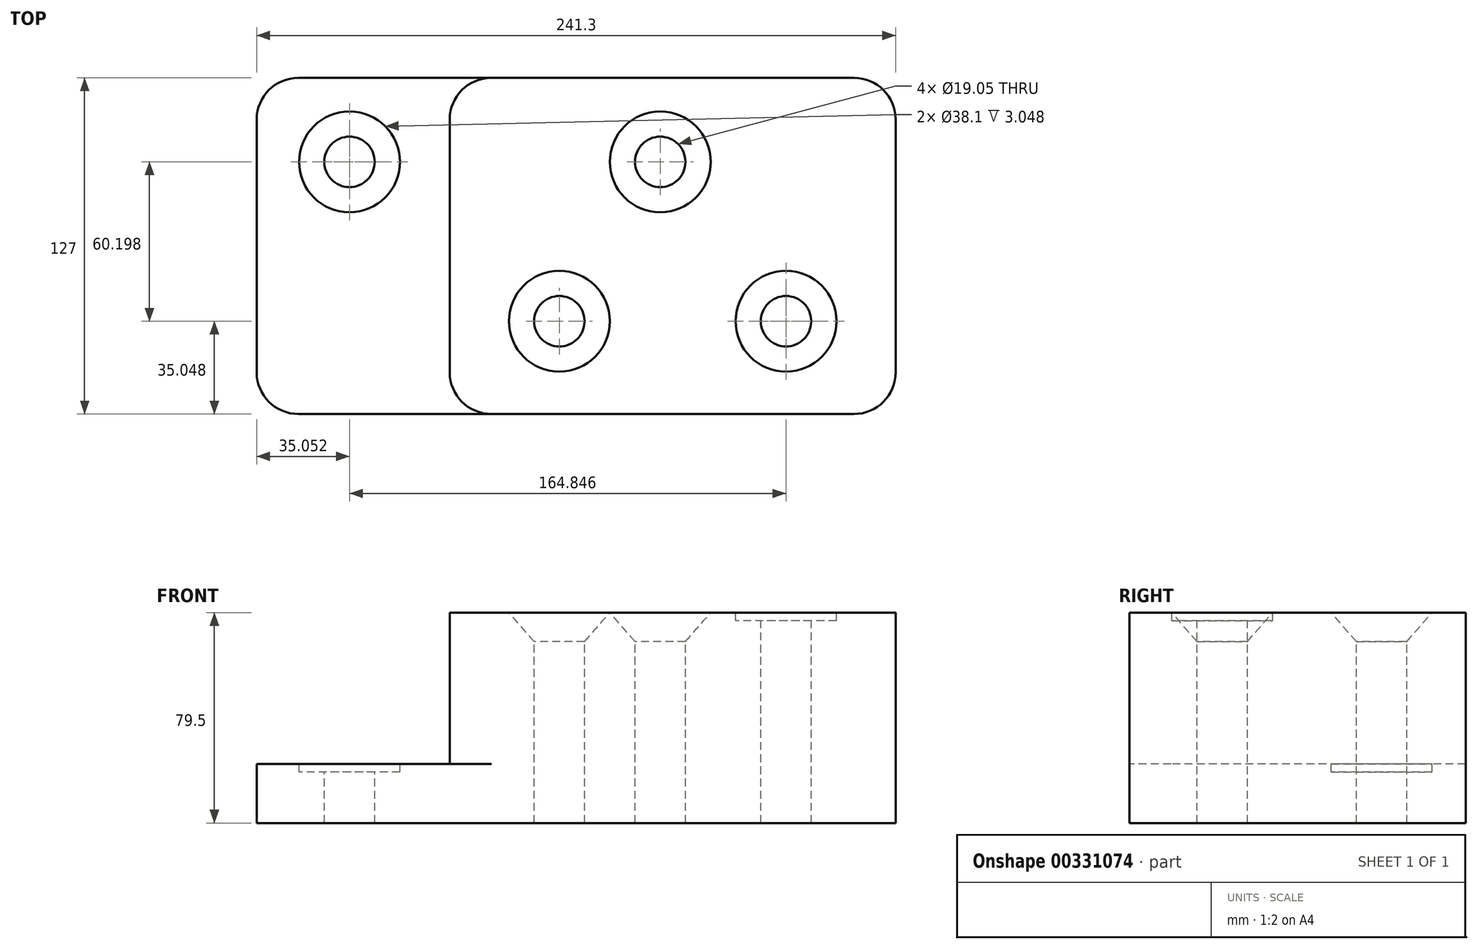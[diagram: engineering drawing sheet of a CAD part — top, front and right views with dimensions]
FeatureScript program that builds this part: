
annotation { "Feature Type Name" : "Feature", "Feature Type Description" : "" }
export const myFeature = defineFeature(function(context is Context, id is Id, definition is map)
    precondition{}
    {
        {
            var Q0;
            Q0=qCreatedBy(makeId("Top.planeOp"),FACE);
            var sketch = newSketch(context, id + "F0", { "sketchPlane" : qUnion([Q0])});
            skLineSegment(sketch, "E0.bottom", {"start": v(-178.85, 101.87) * mm, "end": v(62.45, 101.87) * mm});
            skLineSegment(sketch, "E0.top", {"start": v(-178.85, -25.13) * mm, "end": v(62.45, -25.13) * mm});
            skLineSegment(sketch, "E0.left", {"start": v(-178.85, 101.87) * mm, "end": v(-178.85, -25.13) * mm});
            skLineSegment(sketch, "E0.right", {"start": v(62.45, 101.87) * mm, "end": v(62.45, -25.13) * mm});
            skSolve(sketch);
        }
        {
            var Q0;
            Q0 = qSketchRegion(id + "F0", true);
            extrude(context, id + "F1", {"entities" : qUnion([Q0]), "depth" : 22.35 * mm});
        }
        {
            var Q0;
            Q0=makeQuery(id+"F1.opExtrude","CAP_FACE",FACE,{"disambiguationData":[OSD([sQuery(id+"F0.wireOp",EDGE,"E0.bottom"),sQuery(id+"F0.wireOp",EDGE,"E0.top"),sQuery(id+"F0.wireOp",EDGE,"E0.left"),sQuery(id+"F0.wireOp",EDGE,"E0.right")])],"isStart":false});
            var sketch = newSketch(context, id + "F2", { "sketchPlane" : qUnion([Q0])});
            skLineSegment(sketch, "E1", {"start": v(62.45, 101.87) * mm, "end": v(-105.95, 101.87) * mm});
            skLineSegment(sketch, "E2", {"start": v(-105.95, 101.87) * mm, "end": v(-105.95, -25.13) * mm});
            skLineSegment(sketch, "E3", {"start": v(-105.95, -25.13) * mm, "end": v(62.45, -25.13) * mm});
            skLineSegment(sketch, "E4", {"start": v(62.45, -25.13) * mm, "end": v(62.45, 101.87) * mm});
            skSolve(sketch);
        }
        {
            var Q0;
            Q0 = qSketchRegion(id + "F2", true);
            extrude(context, id + "F3", {"entities" : qUnion([Q0]), "operationType" : NewBodyOperationType.ADD, "depth" : 57.15 * mm});
        }
        {
            var Q0;
            Q0=makeQuery(id+"F1.opExtrude","CAP_FACE",FACE,{"disambiguationData":[OSD([sQuery(id+"F0.wireOp",EDGE,"E0.bottom"),sQuery(id+"F0.wireOp",EDGE,"E0.top"),sQuery(id+"F0.wireOp",EDGE,"E0.left"),sQuery(id+"F0.wireOp",EDGE,"E0.right")])],"isStart":false});
            var sketch = newSketch(context, id + "F4", { "sketchPlane" : qUnion([Q0])});
            skPoint(sketch, "E5", {"position": v(-143.8, 70.12) * mm});
            skSolve(sketch);
        }
        {
            var Q0;
            Q0=makeQuery(id+"F3.opExtrude","CAP_FACE",FACE,{"disambiguationData":[OSD([sQuery(id+"F2.wireOp",EDGE,"E1"),sQuery(id+"F2.wireOp",EDGE,"E2"),sQuery(id+"F2.wireOp",EDGE,"E3"),sQuery(id+"F2.wireOp",EDGE,"E4")])],"isStart":false});
            var sketch = newSketch(context, id + "F5", { "sketchPlane" : qUnion([Q0])});
            skPoint(sketch, "E6", {"position": v(-26.45, 70.12) * mm});
            skPoint(sketch, "E7", {"position": v(-64.55, 9.92) * mm});
            skPoint(sketch, "E8", {"position": v(21.05, 9.92) * mm});
            skSolve(sketch);
        }
        {
            var Q0;
            Q0=sQuery(id+"F4.wireOp",VERTEX,"E5");
            var Q1;
            Q1=sQuery(id+"F5.wireOp",VERTEX,"E8");
            var Q2;
            Q2=makeQuery(id+"F1.opExtrude","SWEPT_BODY",BODY,{"disambiguationData":[OSD([sQuery(id+"F0.wireOp",EDGE,"E0.bottom"),sQuery(id+"F0.wireOp",EDGE,"E0.top"),sQuery(id+"F0.wireOp",EDGE,"E0.left"),sQuery(id+"F0.wireOp",EDGE,"E0.right")])]});
            hole(context, id + "F6", {"style" : HoleStyle.C_BORE, "endStyle" : HoleEndStyle.THROUGH, "holeDiameter" : 19.05 * mm, "cBoreDiameter" : 38.1 * mm, "cBoreDepth" : 3.05 * mm, "tappedDepth" : 12.7 * mm, "tapClearance" : 3, "locations" : qUnion([Q0, Q1]), "scope" : qUnion([Q2])});
        }
        {
            var Q0;
            Q0=sQuery(id+"F5.wireOp",VERTEX,"E6");
            var Q1;
            Q1=sQuery(id+"F5.wireOp",VERTEX,"E7");
            var Q2;
            Q2=makeQuery(id+"F1.opExtrude","SWEPT_BODY",BODY,{"disambiguationData":[OSD([sQuery(id+"F0.wireOp",EDGE,"E0.bottom"),sQuery(id+"F0.wireOp",EDGE,"E0.top"),sQuery(id+"F0.wireOp",EDGE,"E0.left"),sQuery(id+"F0.wireOp",EDGE,"E0.right")])]});
            hole(context, id + "F7", {"style" : HoleStyle.C_SINK, "endStyle" : HoleEndStyle.THROUGH, "holeDiameter" : 19.05 * mm, "cSinkDiameter" : 38.1 * mm, "cSinkAngle" : 82 * degree, "tappedDepth" : 12.7 * mm, "tapClearance" : 3, "locations" : qUnion([Q0, Q1]), "scope" : qUnion([Q2])});
        }
        {
            var Q0;
            Q0=makeQuery(id+"F3.opExtrude","SWEPT_EDGE",EDGE,{"disambiguationData":[OSD([sQuery(id+"F0.wireOp",EDGE,"E0.top"),sQuery(id+"F2.wireOp",EDGE,"E2"),sQuery(id+"F2.wireOp",EDGE,"E3")])]});
            var Q1;
            Q1=makeQuery(id+"F3.opExtrude","SWEPT_EDGE",EDGE,{"disambiguationData":[OSD([sQuery(id+"F0.wireOp",EDGE,"E0.bottom"),sQuery(id+"F2.wireOp",EDGE,"E1"),sQuery(id+"F2.wireOp",EDGE,"E2")])]});
            var Q2;
            Q2=makeQuery(id+"F1.opExtrude","SWEPT_EDGE",EDGE,{"disambiguationData":[OSD([sQuery(id+"F0.wireOp",EDGE,"E0.bottom"),sQuery(id+"F0.wireOp",EDGE,"E0.left")])]});
            var Q3;
            Q3=makeQuery(id+"F1.opExtrude","SWEPT_EDGE",EDGE,{"disambiguationData":[OSD([sQuery(id+"F0.wireOp",EDGE,"E0.top"),sQuery(id+"F0.wireOp",EDGE,"E0.left")])]});
            fillet(context, id + "F8", {"entities" : qUnion([Q0, Q1, Q2, Q3]), "radius" : 15.75 * mm, "tangentPropagation" : true, "allowEdgeOverflow" : false});
        }
        {
            var Q0;
            Q0=makeQuery(id+"F3.boolean.opBoolean","MERGE",EDGE,{"derivedFrom":[makeQuery(id+"F1.opExtrude","SWEPT_EDGE",EDGE,{"disambiguationData":[OSD([sQuery(id+"F0.wireOp",EDGE,"E0.top"),sQuery(id+"F0.wireOp",EDGE,"E0.right")])]}),makeQuery(id+"F3.opExtrude","SWEPT_EDGE",EDGE,{"disambiguationData":[OSD([sQuery(id+"F2.wireOp",EDGE,"E3"),sQuery(id+"F2.wireOp",EDGE,"E4")])]})]});
            var Q1;
            Q1=makeQuery(id+"F3.boolean.opBoolean","MERGE",EDGE,{"derivedFrom":[makeQuery(id+"F1.opExtrude","SWEPT_EDGE",EDGE,{"disambiguationData":[OSD([sQuery(id+"F0.wireOp",EDGE,"E0.bottom"),sQuery(id+"F0.wireOp",EDGE,"E0.right")])]}),makeQuery(id+"F3.opExtrude","SWEPT_EDGE",EDGE,{"disambiguationData":[OSD([sQuery(id+"F2.wireOp",EDGE,"E1"),sQuery(id+"F2.wireOp",EDGE,"E4")])]})]});
            fillet(context, id + "F9", {"entities" : qUnion([Q0, Q1]), "radius" : 15.75 * mm, "tangentPropagation" : true, "allowEdgeOverflow" : false});
        }
    });
